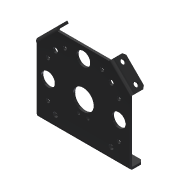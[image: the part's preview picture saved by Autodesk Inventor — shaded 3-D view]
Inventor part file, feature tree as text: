
AUTODESK INVENTOR PART (.ipt)
format: ipt  version: 2013 (Build 170138000, 138)  size: 141,824 bytes
history: native  units: in
note: dims shown in document units (in); Inventor stores cm internally (conversion verified against a paired STEP export)
features: chamfer x1, other x1, imported_body x1
ambient origin geometry x8: Origin, YZ Plane, XZ Plane, XY Plane, X Axis, Y Axis, Z Axis, Center Point
feature tree (3):
  chamfer  "Chamfer1"  [1 undecoded]
  other  "217-2745-001 Rev11"
  imported_body  "Base1"
note: 1 required parameter value undecoded (feature->parameter linkage not recoverable at this tier; creation-order binding heuristic only, values carry confidence <= 0.55)
